annotation { "Feature Type Name" : "Feature", "Feature Type Description" : "" }
export const myFeature = defineFeature(function(context is Context, id is Id, definition is map)
    precondition{}
    {
        {
            var Q0;
            Q0=qCreatedBy(makeId("Top.planeOp"),FACE);
            var sketch = newSketch(context, id + "F0", { "sketchPlane" : qUnion([Q0])});
            skLineSegment(sketch, "E0.bottom", {"start": v(10, 41.94) * mm, "end": v(90, 41.94) * mm});
            skLineSegment(sketch, "E0.top", {"start": v(10, 1.94) * mm, "end": v(90, 1.94) * mm});
            skLineSegment(sketch, "E0.left", {"start": v(0, 31.94) * mm, "end": v(0, 11.94) * mm});
            skLineSegment(sketch, "E0.right", {"start": v(100, 31.94) * mm, "end": v(100, 11.94) * mm});
            skPoint(sketch, "E1.visualSharp", {"position": v(0, 41.94) * mm});
            skArc(sketch, "E1.filletArc", {"start": v(10, 41.94) * mm, "mid": v(2.93, 39.01) * mm, "end": v(0, 31.94) * mm});
            skPoint(sketch, "E2.visualSharp", {"position": v(0, 1.94) * mm});
            skArc(sketch, "E2.filletArc", {"start": v(0, 11.94) * mm, "mid": v(2.93, 4.87) * mm, "end": v(10, 1.94) * mm});
            skPoint(sketch, "E3.visualSharp", {"position": v(100, 41.94) * mm});
            skArc(sketch, "E3.filletArc", {"start": v(100, 31.94) * mm, "mid": v(97.07, 39.01) * mm, "end": v(90, 41.94) * mm});
            skPoint(sketch, "E4.visualSharp", {"position": v(100, 1.94) * mm});
            skArc(sketch, "E4.filletArc", {"start": v(90, 1.94) * mm, "mid": v(97.07, 4.87) * mm, "end": v(100, 11.94) * mm});
            skCircle(sketch, "E5", {"center": v(7.62, 33.88) * mm, "radius": 3.23 * mm});
            skText(sketch, "E6", { "text": "Heidi Chang", "fontName": "OpenSans-Regular.ttf"});
            const initialGuessF0  = {"E6": [0.01188, 0.01711, 1, 0, 0.01014]};
            skSetInitialGuess(sketch, initialGuessF0);
            skSolve(sketch);
        }
        {
            var Q0;
            Q0=makeQuery(id+"F0.imprint","IMPRINT",FACE,{"disambiguationData":[TD([[makeQuery(id+"F0.imprint","IMPRINT",EDGE,{"derivedFrom":sQuery(id+"F0.wireOp",EDGE,"E0.bottom")}),-1.0]])]});
            extrude(context, id + "F1", {"entities" : qUnion([Q0]), "depth" : 30 * mm, "offsetDistance" : 25 * mm});
        }
    });